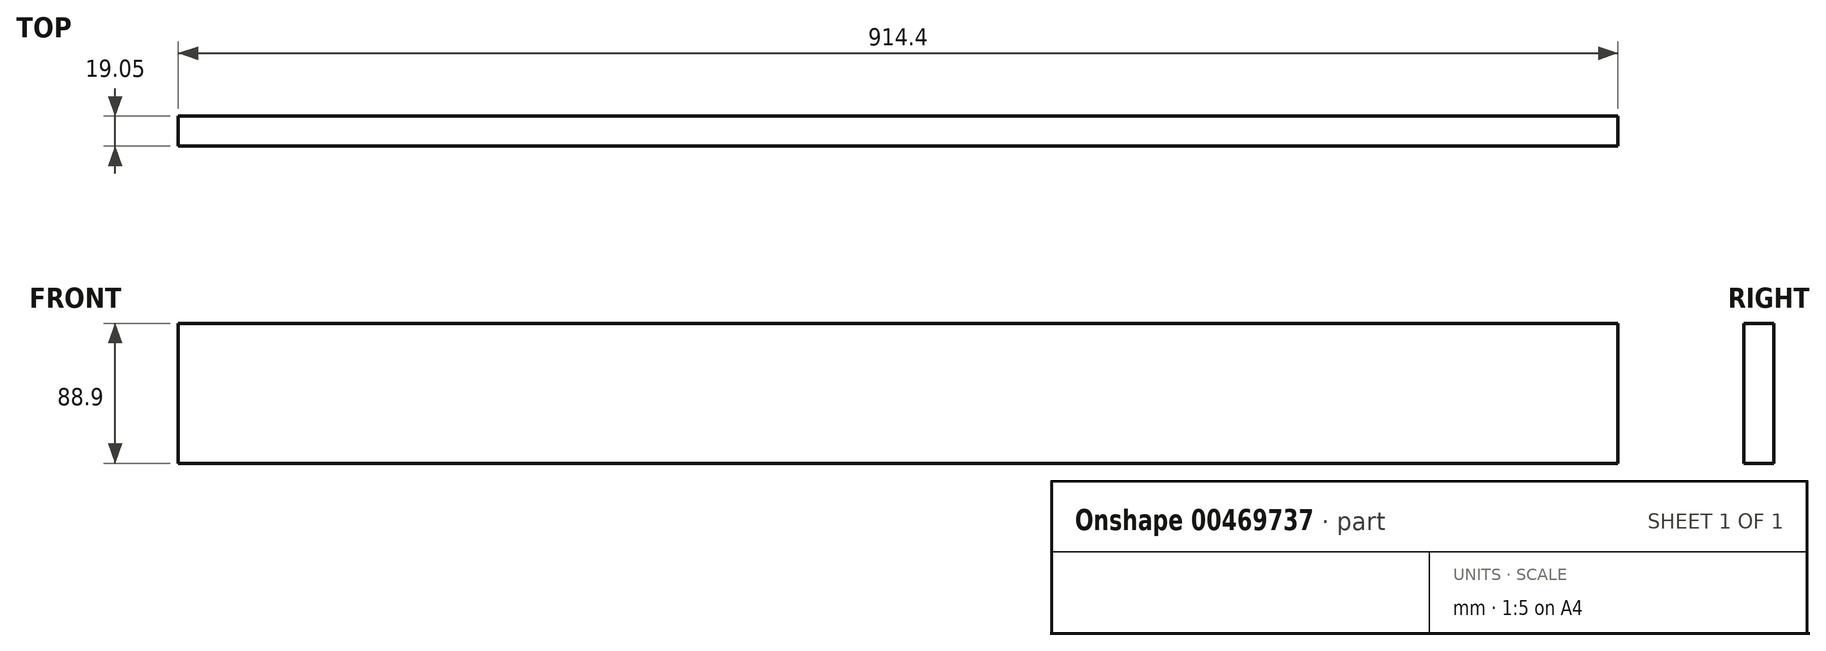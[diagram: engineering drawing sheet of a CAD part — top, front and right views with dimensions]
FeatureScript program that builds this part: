
annotation { "Feature Type Name" : "Feature", "Feature Type Description" : "" }
export const myFeature = defineFeature(function(context is Context, id is Id, definition is map)
    precondition{}
    {
        {
            var Q0;
            Q0=qCreatedBy(makeId("Front.planeOp"),FACE);
            var sketch = newSketch(context, id + "F0", { "sketchPlane" : qUnion([Q0])});
            skLineSegment(sketch, "E0.bottom", {"start": v(0, 0) * mm, "end": v(914.4, 0) * mm});
            skLineSegment(sketch, "E0.top", {"start": v(0, 88.9) * mm, "end": v(914.4, 88.9) * mm});
            skLineSegment(sketch, "E0.left", {"start": v(0, 0) * mm, "end": v(0, 88.9) * mm});
            skLineSegment(sketch, "E0.right", {"start": v(914.4, 0) * mm, "end": v(914.4, 88.9) * mm});
            skSolve(sketch);
        }
        {
            var Q0;
            Q0=makeQuery(id+"F0.imprint","IMPRINT",FACE,{"disambiguationData":[TD([[makeQuery(id+"F0.imprint","IMPRINT",EDGE,{"derivedFrom":sQuery(id+"F0.wireOp",EDGE,"E0.bottom")}),1.0]])]});
            extrude(context, id + "F1", {"entities" : qUnion([Q0]), "depth" : 19.05 * mm, "offsetDistance" : 25.4 * mm});
        }
    });
